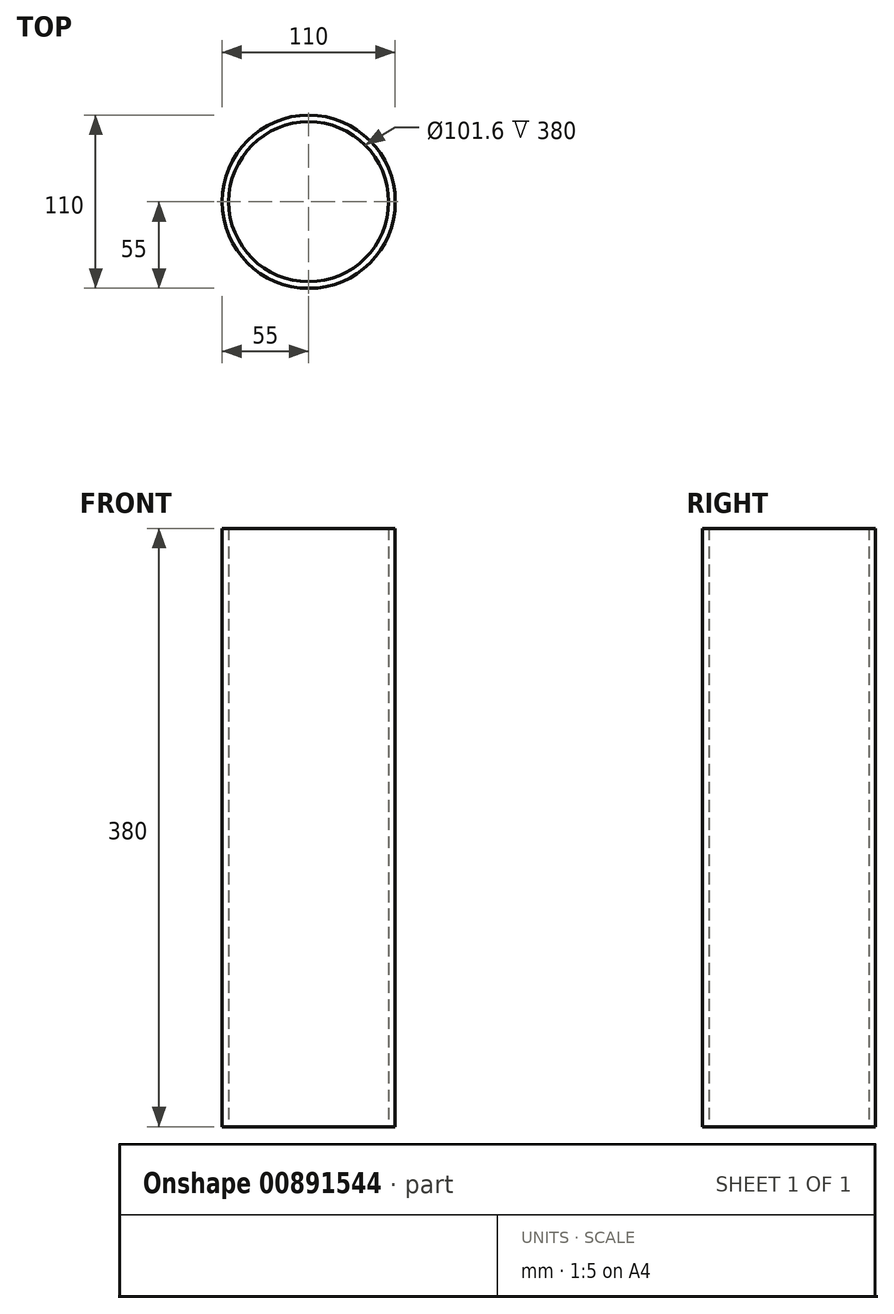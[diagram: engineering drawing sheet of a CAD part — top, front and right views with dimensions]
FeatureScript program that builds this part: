
annotation { "Feature Type Name" : "Feature", "Feature Type Description" : "" }
export const myFeature = defineFeature(function(context is Context, id is Id, definition is map)
    precondition{}
    {
        {
            var Q0;
            Q0=qCreatedBy(makeId("Top.planeOp"),FACE);
            var sketch = newSketch(context, id + "F0", { "sketchPlane" : qUnion([Q0])});
            skCircle(sketch, "E0", {"center": v(0, 0) * mm, "radius": 55 * mm});
            skCircle(sketch, "E1.0", {"center": v(0, 0) * mm, "radius": 50.8 * mm});
            skSolve(sketch);
        }
        {
            var Q0;
            Q0 = qSketchRegion(id + "F0", true);
            extrude(context, id + "F1", {"entities" : qUnion([Q0]), "depth" : 380 * mm, "offsetDistance" : 25 * mm});
        }
    });
